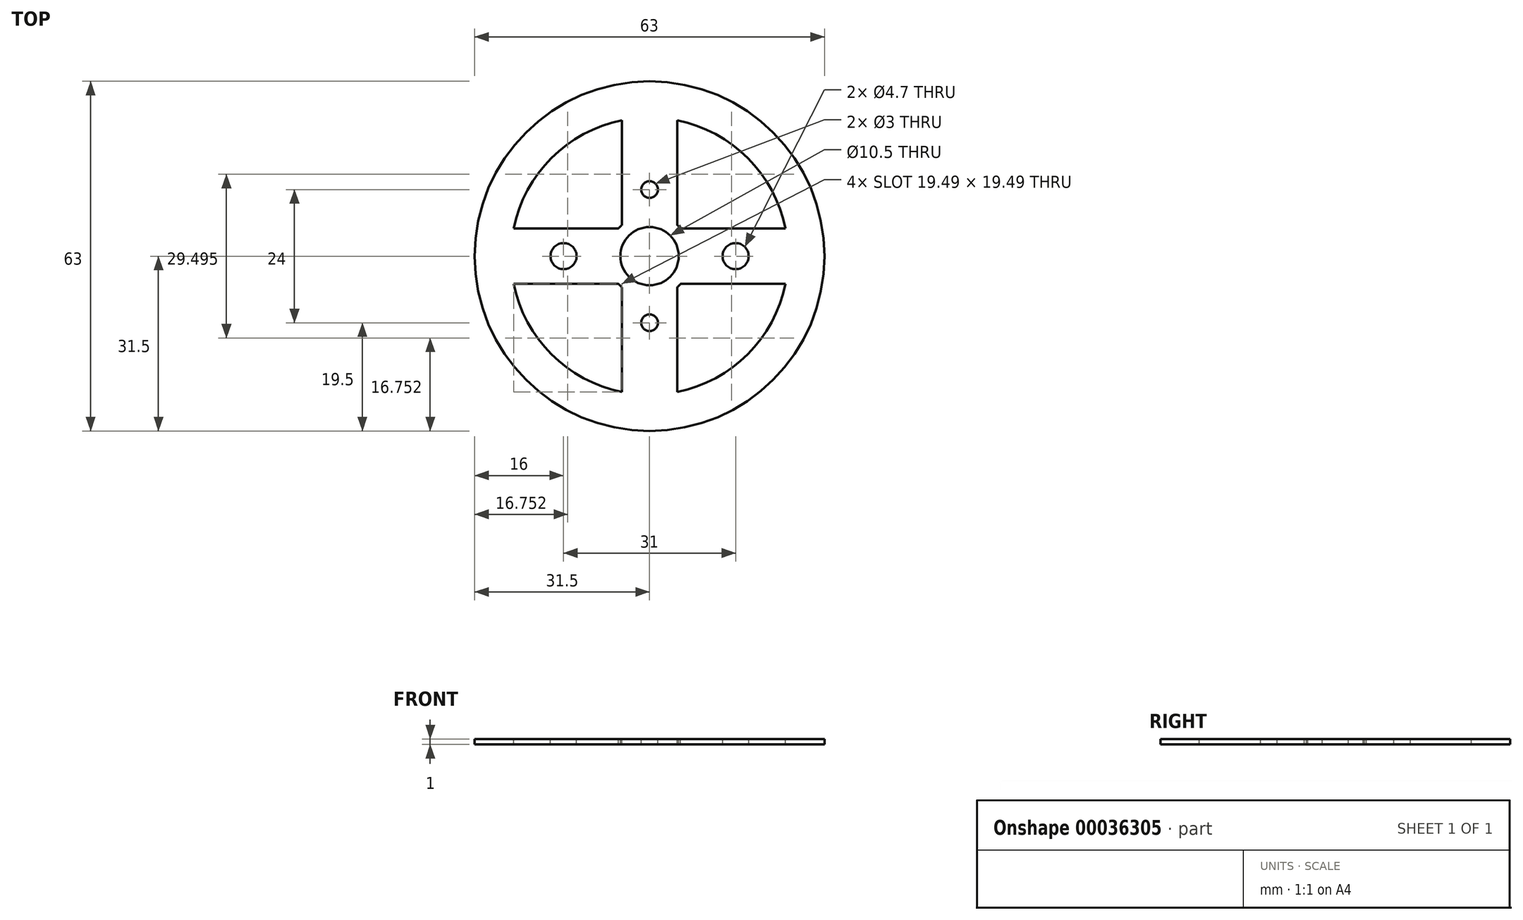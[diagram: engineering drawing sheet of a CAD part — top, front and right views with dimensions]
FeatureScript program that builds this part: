
annotation { "Feature Type Name" : "Feature", "Feature Type Description" : "" }
export const myFeature = defineFeature(function(context is Context, id is Id, definition is map)
    precondition{}
    {
        {
            var Q0;
            Q0=qCreatedBy(makeId("Top.planeOp"),FACE);
            var sketch = newSketch(context, id + "F0", { "sketchPlane" : qUnion([Q0])});
            skCircle(sketch, "E0", {"center": v(0, 0) * mm, "radius": 31.5 * mm});
            skSolve(sketch);
        }
        {
            var Q0;
            Q0=qSketchRegion(id+"F0",true);
            extrude(context, id + "F1", {"entities" : qUnion([Q0]), "depth" : 1 * mm});
        }
        {
            var Q0;
            Q0=makeQuery(id+"F1.opExtrude","CAP_FACE",FACE,{"disambiguationData":[OSD([sQuery(id+"F0.wireOp",EDGE,"E0")])],"isStart":false});
            var sketch = newSketch(context, id + "F2", { "sketchPlane" : qUnion([Q0])});
            skCircle(sketch, "E1", {"center": v(0, 0) * mm, "radius": 5.25 * mm});
            skSolve(sketch);
        }
        {
            var Q0;
            Q0=makeQuery(id+"F2.imprint","IMPRINT",FACE,{"disambiguationData":[TD([[makeQuery(id+"F2.imprint","IMPRINT",EDGE,{"derivedFrom":sQuery(id+"F2.wireOp",EDGE,"E1")}),1.0]])]});
            extrude(context, id + "F3", {"entities" : qUnion([Q0]), "operationType" : NewBodyOperationType.REMOVE, "endBound" : BoundingType.UP_TO_NEXT, "oppositeDirection" : true, "depth" : 25 * mm});
        }
        {
            var Q0;
            Q0=makeQuery(id+"F1.opExtrude","CAP_FACE",FACE,{"disambiguationData":[OSD([sQuery(id+"F0.wireOp",EDGE,"E0")])],"isStart":false});
            var sketch = newSketch(context, id + "F4", { "sketchPlane" : qUnion([Q0])});
            skCircle(sketch, "E2", {"center": v(0, 0) * mm, "radius": 25 * mm});
            skCircle(sketch, "E3", {"center": v(0, 0) * mm, "radius": 7.5 * mm});
            skLineSegment(sketch, "E4", {"start": v(0, -7.5) * mm, "end": v(0, -25) * mm, "construction": true});
            skLineSegment(sketch, "E5", {"start": v(-7.5, 0) * mm, "end": v(-25, 0) * mm, "construction": true});
            skLineSegment(sketch, "E6", {"start": v(0, 7.5) * mm, "end": v(0, 25) * mm, "construction": true});
            skLineSegment(sketch, "E7", {"start": v(7.5, 0) * mm, "end": v(25, 0) * mm, "construction": true});
            skLineSegment(sketch, "E8.0", {"start": v(5, 5.6) * mm, "end": v(5, 24.5) * mm});
            skLineSegment(sketch, "E9.0", {"start": v(-5, 5.6) * mm, "end": v(-5, 24.5) * mm});
            skLineSegment(sketch, "E10", {"start": v(5, -5.6) * mm, "end": v(5, -24.5) * mm});
            skLineSegment(sketch, "E11", {"start": v(-5, -5.6) * mm, "end": v(-5, -24.5) * mm});
            skLineSegment(sketch, "E12.0", {"start": v(5.6, 5) * mm, "end": v(24.5, 5) * mm});
            skLineSegment(sketch, "E13.0", {"start": v(5.6, -5) * mm, "end": v(24.5, -5) * mm});
            skLineSegment(sketch, "E14", {"start": v(-5.6, 5) * mm, "end": v(-24.5, 5) * mm});
            skLineSegment(sketch, "E15", {"start": v(-5.6, -5) * mm, "end": v(-24.5, -5) * mm});
            skLineSegment(sketch, "E16", {"start": v(-25, 0) * mm, "end": v(-31.5, 0) * mm, "construction": true});
            skLineSegment(sketch, "E17", {"start": v(25, 0) * mm, "end": v(31.5, 0) * mm, "construction": true});
            skLineSegment(sketch, "E18", {"start": v(0, 25) * mm, "end": v(0, 31.5) * mm, "construction": true});
            skLineSegment(sketch, "E19", {"start": v(0, -25) * mm, "end": v(0, -31.5) * mm, "construction": true});
            skCircle(sketch, "E20", {"center": v(0, -12) * mm, "radius": 1.5 * mm});
            skCircle(sketch, "E21", {"center": v(0, 12) * mm, "radius": 1.5 * mm});
            skCircle(sketch, "E22", {"center": v(-15.5, 0) * mm, "radius": 2.35 * mm});
            skCircle(sketch, "E23", {"center": v(15.5, 0) * mm, "radius": 2.35 * mm});
            skSolve(sketch);
        }
        {
            var Q0;
            {var subQ1=sQuery(id+"F4.wireOp",EDGE,"E9.0");Q0=makeQuery(id+"F4.imprint","IMPRINT",FACE,{"disambiguationData":[TD([[makeQuery(id+"F4.imprint","IMPRINT",EDGE,{"derivedFrom":subQ1}),1.0]])]});}
            var Q1;
            {var subQ1=sQuery(id+"F4.wireOp",EDGE,"E8.0");Q1=makeQuery(id+"F4.imprint","IMPRINT",FACE,{"disambiguationData":[TD([[makeQuery(id+"F4.imprint","IMPRINT",EDGE,{"derivedFrom":subQ1}),-1.0]])]});}
            var Q2;
            {var subQ1=sQuery(id+"F4.wireOp",EDGE,"E10");Q2=makeQuery(id+"F4.imprint","IMPRINT",FACE,{"disambiguationData":[TD([[makeQuery(id+"F4.imprint","IMPRINT",EDGE,{"derivedFrom":subQ1}),1.0]])]});}
            var Q3;
            {var subQ1=sQuery(id+"F4.wireOp",EDGE,"E11");Q3=makeQuery(id+"F4.imprint","IMPRINT",FACE,{"disambiguationData":[TD([[makeQuery(id+"F4.imprint","IMPRINT",EDGE,{"derivedFrom":subQ1}),-1.0]])]});}
            var Q4;
            Q4=makeQuery(id+"F4.imprint","IMPRINT",FACE,{"disambiguationData":[TD([[makeQuery(id+"F4.imprint","IMPRINT",EDGE,{"derivedFrom":sQuery(id+"F4.wireOp",EDGE,"E20")}),1.0]])]});
            var Q5;
            Q5=makeQuery(id+"F4.imprint","IMPRINT",FACE,{"disambiguationData":[TD([[makeQuery(id+"F4.imprint","IMPRINT",EDGE,{"derivedFrom":sQuery(id+"F4.wireOp",EDGE,"E23")}),1.0]])]});
            var Q6;
            Q6=makeQuery(id+"F4.imprint","IMPRINT",FACE,{"disambiguationData":[TD([[makeQuery(id+"F4.imprint","IMPRINT",EDGE,{"derivedFrom":sQuery(id+"F4.wireOp",EDGE,"E21")}),1.0]])]});
            var Q7;
            Q7=makeQuery(id+"F4.imprint","IMPRINT",FACE,{"disambiguationData":[TD([[makeQuery(id+"F4.imprint","IMPRINT",EDGE,{"derivedFrom":sQuery(id+"F4.wireOp",EDGE,"E22")}),1.0]])]});
            extrude(context, id + "F5", {"entities" : qUnion([Q0, Q1, Q2, Q3, Q4, Q5, Q6, Q7]), "operationType" : NewBodyOperationType.REMOVE, "endBound" : BoundingType.UP_TO_NEXT, "oppositeDirection" : true, "depth" : 25 * mm});
        }
    });
